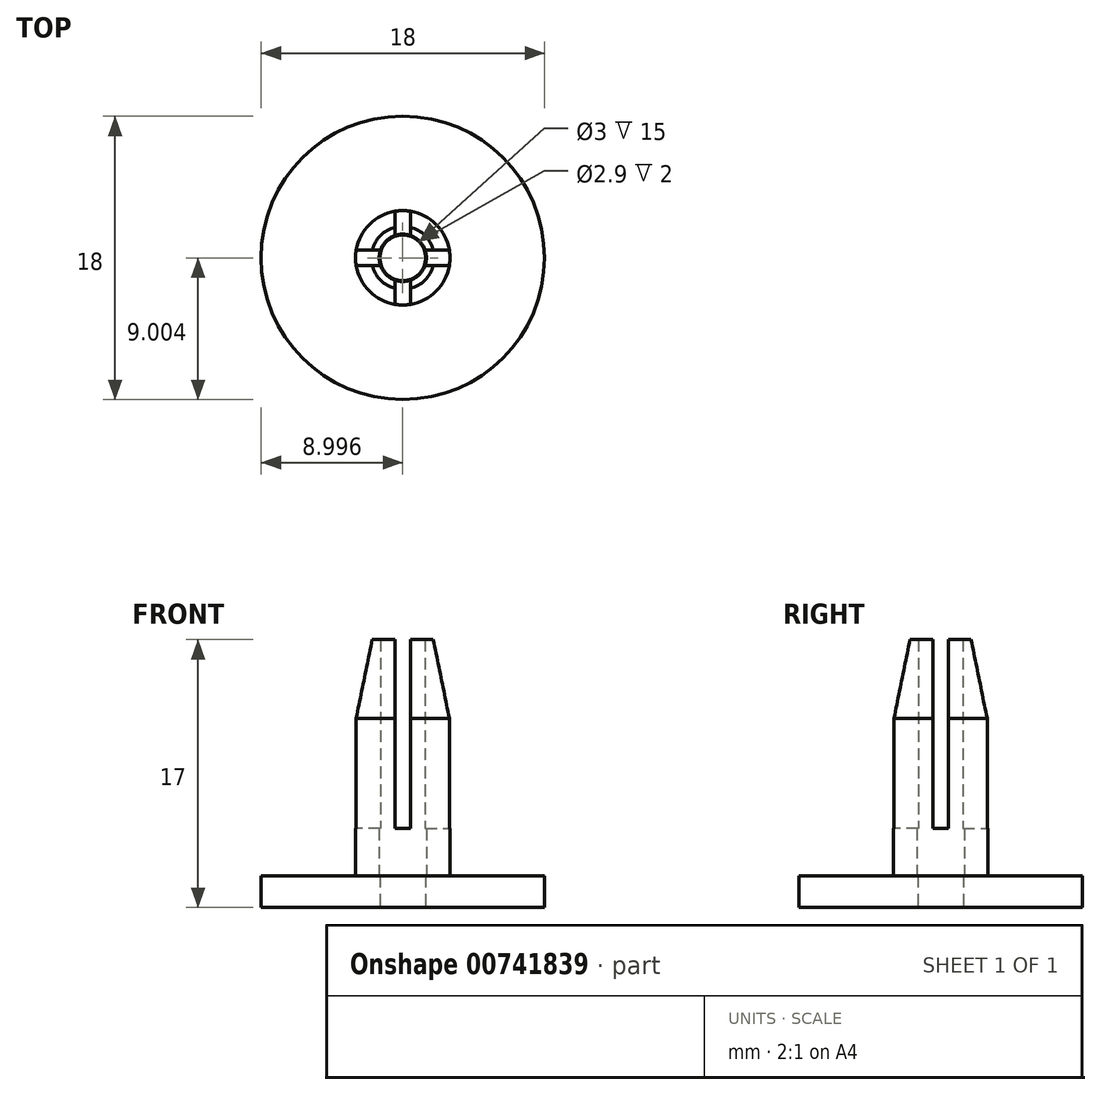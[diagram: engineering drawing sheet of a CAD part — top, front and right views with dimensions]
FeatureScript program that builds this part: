
annotation { "Feature Type Name" : "Feature", "Feature Type Description" : "" }
export const myFeature = defineFeature(function(context is Context, id is Id, definition is map)
    precondition{}
    {
        {
            var Q0;
            Q0=qCreatedBy(makeId("Top.planeOp"),FACE);
            var sketch = newSketch(context, id + "F0", { "sketchPlane" : qUnion([Q0])});
            skCircle(sketch, "E0", {"center": v(-40.05, 19.14) * mm, "radius": 9 * mm});
            skCircle(sketch, "E1", {"center": v(-40.05, 19.14) * mm, "radius": 1.45 * mm});
            skSolve(sketch);
        }
        {
            var Q0;
            Q0 = qSketchRegion(id + "F0", true);
            extrude(context, id + "F1", {"entities" : qUnion([Q0]), "depth" : 2 * mm, "offsetDistance" : 25 * mm});
        }
        {
            var Q0;
            Q0=makeQuery(id+"F1.opExtrude","CAP_FACE",FACE,{"disambiguationData":[OSD([sQuery(id+"F0.wireOp",EDGE,"E0"),sQuery(id+"F0.wireOp",EDGE,"E1")])],"isStart":false});
            var sketch = newSketch(context, id + "F2", { "sketchPlane" : qUnion([Q0])});
            skCircle(sketch, "E2", {"center": v(-40.05, 19.14) * mm, "radius": 3 * mm});
            skCircle(sketch, "E3", {"center": v(-40.05, 19.14) * mm, "radius": 1.5 * mm});
            skSolve(sketch);
        }
        {
            var Q0;
            Q0 = qSketchRegion(id + "F2", true);
            extrude(context, id + "F3", {"entities" : qUnion([Q0]), "operationType" : NewBodyOperationType.ADD, "depth" : 15 * mm, "offsetDistance" : 25 * mm});
        }
        {
            var Q0;
            Q0=makeQuery(id+"F3.opExtrude","CAP_FACE",FACE,{"disambiguationData":[OSD([sQuery(id+"F2.wireOp",EDGE,"E2"),sQuery(id+"F2.wireOp",EDGE,"E3")])],"isStart":false});
            var sketch = newSketch(context, id + "F4", { "sketchPlane" : qUnion([Q0])});
            skLineSegment(sketch, "E4.top", {"start": v(-40.05, 19.64) * mm, "end": v(-36.05, 19.64) * mm});
            skLineSegment(sketch, "E4.right", {"start": v(-36.05, 19.14) * mm, "end": v(-36.05, 19.64) * mm});
            skLineSegment(sketch, "E5.top", {"start": v(-40.05, 23.14) * mm, "end": v(-39.55, 23.14) * mm});
            skLineSegment(sketch, "E5.right", {"start": v(-39.55, 19.14) * mm, "end": v(-39.55, 23.14) * mm});
            skLineSegment(sketch, "E6.MirrorCS", {"start": v(-36.05, 19.14) * mm, "end": v(-36.05, 18.64) * mm});
            skLineSegment(sketch, "E7.MirrorCS", {"start": v(-40.05, 18.64) * mm, "end": v(-36.05, 18.64) * mm});
            skLineSegment(sketch, "E8.MirrorCS", {"start": v(-39.55, 19.14) * mm, "end": v(-39.55, 15.14) * mm});
            skLineSegment(sketch, "E9.MirrorCS", {"start": v(-40.05, 15.14) * mm, "end": v(-39.55, 15.14) * mm});
            skLineSegment(sketch, "E10.MirrorCS", {"start": v(-40.55, 19.14) * mm, "end": v(-40.55, 23.14) * mm});
            skLineSegment(sketch, "E11.MirrorCS", {"start": v(-40.05, 23.14) * mm, "end": v(-40.55, 23.14) * mm});
            skLineSegment(sketch, "E12.MirrorCS", {"start": v(-40.05, 19.64) * mm, "end": v(-44.05, 19.64) * mm});
            skLineSegment(sketch, "E13.MirrorCS", {"start": v(-44.05, 19.14) * mm, "end": v(-44.05, 19.64) * mm});
            skLineSegment(sketch, "E14.MirrorCS", {"start": v(-40.05, 18.64) * mm, "end": v(-44.05, 18.64) * mm});
            skLineSegment(sketch, "E15.MirrorCS", {"start": v(-44.05, 19.14) * mm, "end": v(-44.05, 18.64) * mm});
            skLineSegment(sketch, "E16.MirrorCS", {"start": v(-40.55, 19.14) * mm, "end": v(-40.55, 15.14) * mm});
            skLineSegment(sketch, "E17.MirrorCS", {"start": v(-40.05, 15.14) * mm, "end": v(-40.55, 15.14) * mm});
            skPoint(sketch, "E18.orphan", {"position": v(-40.05, 15.14) * mm});
            skPoint(sketch, "E4.left.start.orphan", {"position": v(-40.05, 19.14) * mm});
            skSolve(sketch);
        }
        {
            var Q0;
            Q0=makeQuery(id+"F3.opExtrude","CAP_EDGE",EDGE,{"disambiguationData":[OSD([sQuery(id+"F2.wireOp",EDGE,"E2")])],"isStart":false});
            chamfer(context, id + "F5", {"entities" : qUnion([Q0]), "chamferType" : ChamferType.TWO_OFFSETS, "width1" : 1 * mm, "oppositeDirection" : false, "width2" : 5 * mm, "tangentPropagation" : true});
        }
        {
            var Q0;
            Q0 = qSketchRegion(id + "F4", true);
            extrude(context, id + "F6", {"entities" : qUnion([Q0]), "operationType" : NewBodyOperationType.REMOVE, "oppositeDirection" : true, "depth" : 12 * mm, "offsetDistance" : 25 * mm});
        }
    });
